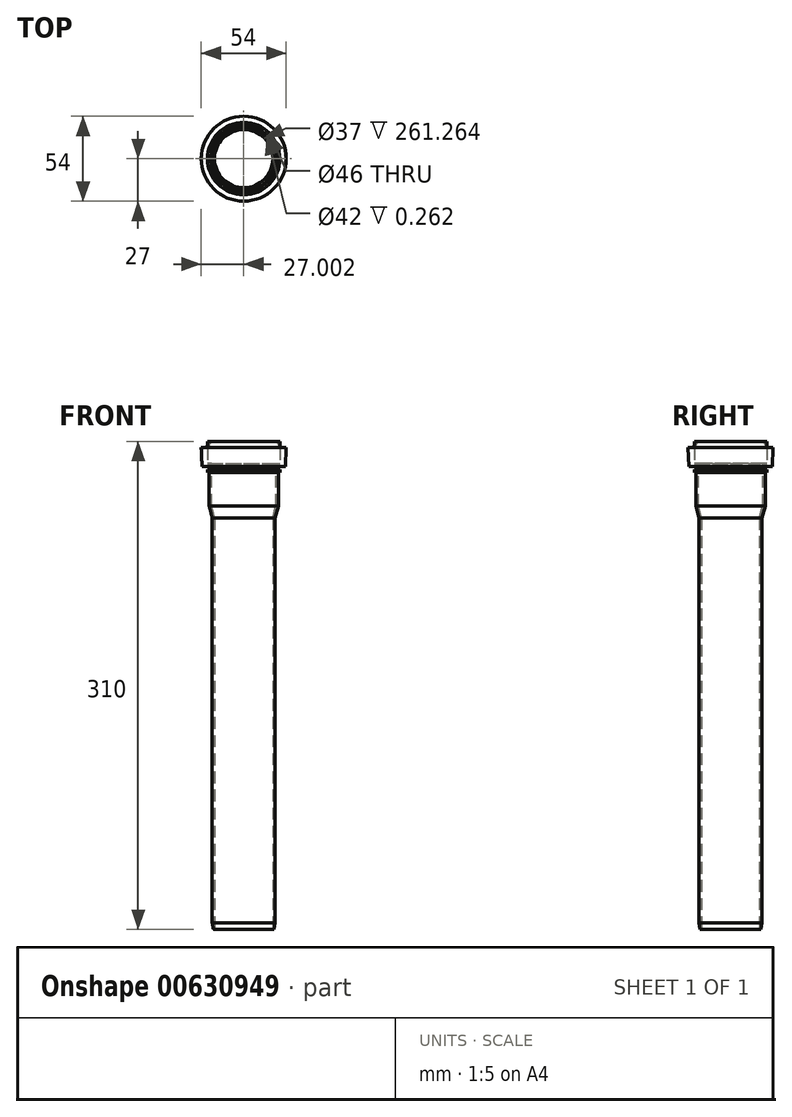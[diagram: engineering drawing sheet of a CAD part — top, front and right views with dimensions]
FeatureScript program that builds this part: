
annotation { "Feature Type Name" : "Feature", "Feature Type Description" : "" }
export const myFeature = defineFeature(function(context is Context, id is Id, definition is map)
    precondition{}
    {
        {
            var Q0;
            Q0=qCreatedBy(makeId("Front.planeOp"),FACE);
            var sketch = newSketch(context, id + "F0", { "sketchPlane" : qUnion([Q0])});
            skLineSegment(sketch, "E0", {"start": v(21.1, -63.46) * mm, "end": v(21.1, 11.84) * mm});
            skLineSegment(sketch, "E1", {"start": v(-0.9, 2.56) * mm, "end": v(-0.9, -18.44) * mm});
            skLineSegment(sketch, "E2", {"start": v(-0.9, -18.44) * mm, "end": v(1.1, -26.18) * mm});
            skLineSegment(sketch, "E3", {"start": v(-0.9, 2.56) * mm, "end": v(-1.9, 2.56) * mm});
            skLineSegment(sketch, "E4", {"start": v(-1.9, 2.56) * mm, "end": v(-1.9, 4.56) * mm});
            skLineSegment(sketch, "E5", {"start": v(-1.9, 4.56) * mm, "end": v(-0.9, 4.56) * mm});
            skLineSegment(sketch, "E6", {"start": v(-0.9, 4.56) * mm, "end": v(-0.9, 6.56) * mm});
            skLineSegment(sketch, "E7", {"start": v(-0.9, 6.56) * mm, "end": v(-5.4, 6.56) * mm});
            skLineSegment(sketch, "E8", {"start": v(-5.4, 6.56) * mm, "end": v(-5.9, 18.55) * mm});
            skLineSegment(sketch, "E9", {"start": v(-5.9, 18.55) * mm, "end": v(-3.9, 18.55) * mm});
            skLineSegment(sketch, "E10", {"start": v(-1.9, 20.55) * mm, "end": v(-1.9, 22.55) * mm});
            skLineSegment(sketch, "E11", {"start": v(-1.9, 22.55) * mm, "end": v(0.1, 22.55) * mm});
            skLineSegment(sketch, "E12", {"start": v(-1.9, 8.56) * mm, "end": v(-1.9, 18.24) * mm});
            skLineSegment(sketch, "E13", {"start": v(-1.9, 8.56) * mm, "end": v(0.6, 8.57) * mm});
            skPoint(sketch, "E14.visualSharp", {"position": v(-1.9, 18.55) * mm});
            skArc(sketch, "E14.filletArc", {"start": v(-3.9, 18.55) * mm, "mid": v(-2.48, 19.14) * mm, "end": v(-1.9, 20.55) * mm});
            skLineSegment(sketch, "E15", {"start": v(1.1, -26.18) * mm, "end": v(2.6, -26.18) * mm});
            skLineSegment(sketch, "E16", {"start": v(0.63, -18.4) * mm, "end": v(0.6, 8.57) * mm});
            skLineSegment(sketch, "E17", {"start": v(2.6, -26.18) * mm, "end": v(0.63, -18.4) * mm});
            skLineSegment(sketch, "E18", {"start": v(0.1, 22.55) * mm, "end": v(0.1, 22.3) * mm});
            skLineSegment(sketch, "E19", {"start": v(0.1, 22.3) * mm, "end": v(-1.9, 18.24) * mm});
            skLineSegment(sketch, "E20", {"start": v(2.6, -26.18) * mm, "end": v(2.6, -32.45) * mm});
            skLineSegment(sketch, "E21", {"start": v(2.6, -32.45) * mm, "end": v(1.1, -32.45) * mm});
            skLineSegment(sketch, "E22", {"start": v(1.1, -32.45) * mm, "end": v(1.1, -26.18) * mm});
            skSolve(sketch);
        }
        {
            var Q0;
            Q0=makeQuery(id+"F0.imprint","IMPRINT",FACE,{"disambiguationData":[TD([[makeQuery(id+"F0.imprint","IMPRINT",EDGE,{"derivedFrom":sQuery(id+"F0.wireOp",EDGE,"E1")}),1.0]])]});
            var Q1;
            Q1=makeQuery(id+"F0.imprint","IMPRINT",FACE,{"disambiguationData":[TD([[makeQuery(id+"F0.imprint","IMPRINT",EDGE,{"derivedFrom":sQuery(id+"F0.wireOp",EDGE,"E15")}),-1.0]])]});
            var Q2;
            Q2=sQuery(id+"F0.wireOp",EDGE,"E0");
            revolve(context, id + "F1", {"entities" : qUnion([Q0, Q1]), "axis" : qUnion([Q2]), "revolveType" : RevolveType.FULL});
        }
        {
            var Q0;
            Q0=makeQuery(id+"F1.opRevolve","SWEPT_FACE",FACE,{"disambiguationData":[OSD([sQuery(id+"F0.wireOp",EDGE,"E21")])]});
            extrude(context, id + "F2", {"entities" : qUnion([Q0]), "operationType" : NewBodyOperationType.ADD, "depth" : 255 * mm, "offsetDistance" : 25 * mm});
        }
        {
            var Q0;
            Q0=makeQuery(id+"F2.opExtrude","CAP_EDGE",EDGE,{"disambiguationData":[OSD([sQuery(id+"F0.wireOp",EDGE,"E21"),sQuery(id+"F0.wireOp",EDGE,"E22")])],"isStart":false});
            chamfer(context, id + "F3", {"entities" : qUnion([Q0]), "chamferType" : ChamferType.OFFSET_ANGLE, "width" : 4 * mm, "oppositeDirection" : true, "angle" : 10 * degree, "tangentPropagation" : true});
        }
    });
